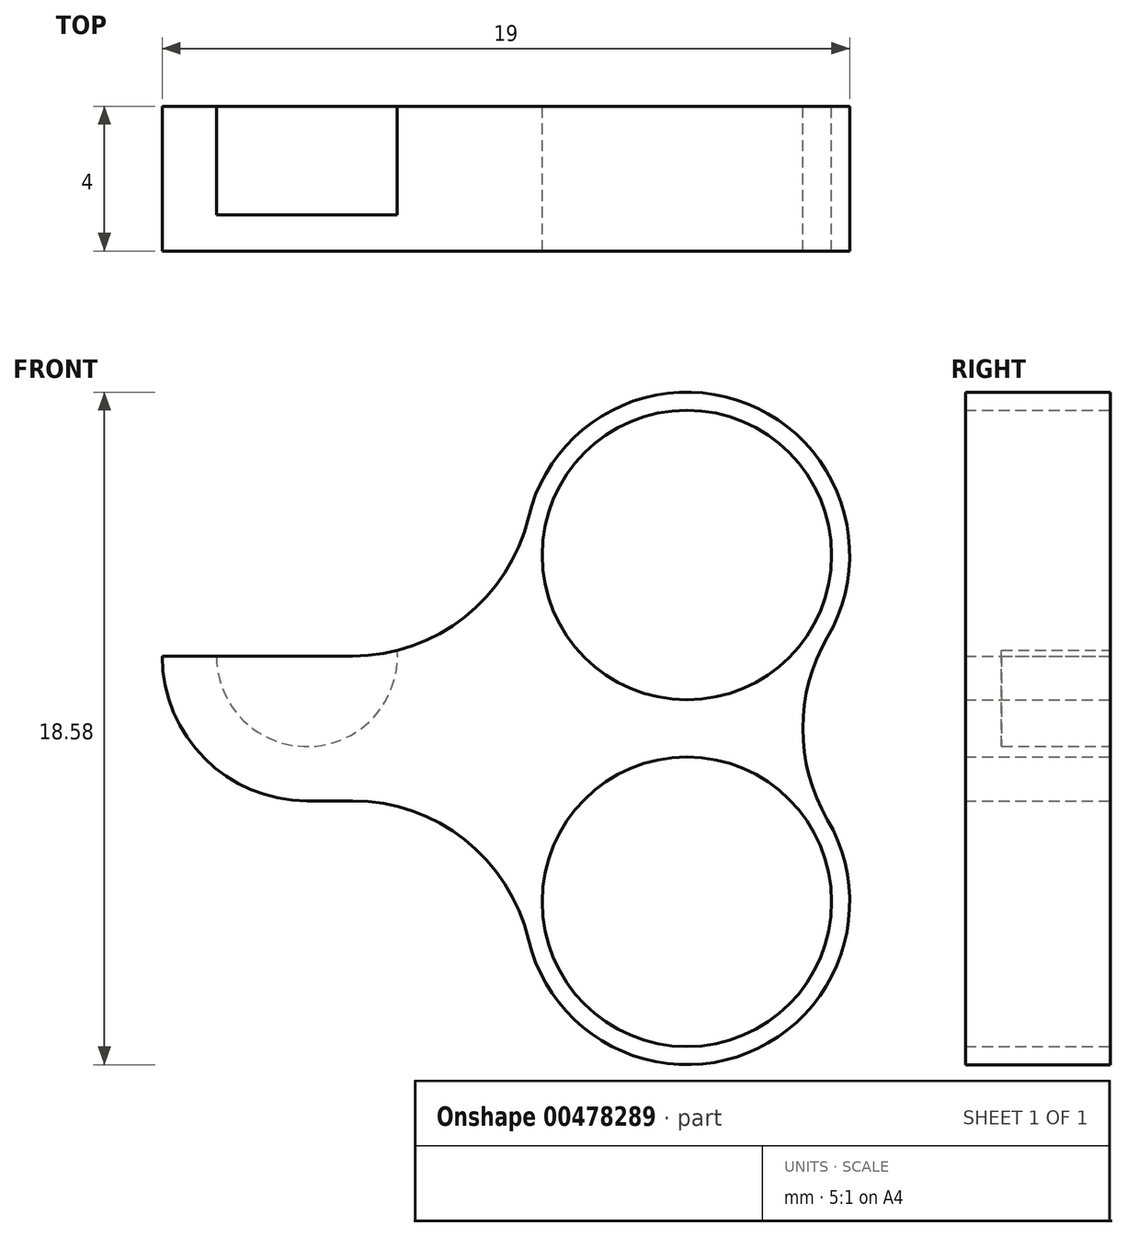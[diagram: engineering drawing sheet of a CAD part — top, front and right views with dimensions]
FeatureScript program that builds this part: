
annotation { "Feature Type Name" : "Feature", "Feature Type Description" : "" }
export const myFeature = defineFeature(function(context is Context, id is Id, definition is map)
    precondition{}
    {
        {
            var Q0;
            Q0=qCreatedBy(makeId("Front.planeOp"),FACE);
            var sketch = newSketch(context, id + "F0", { "sketchPlane" : qUnion([Q0])});
            skLineSegment(sketch, "E0.bottom", {"start": v(-4.5, 4.5) * mm, "end": v(4.5, 4.5) * mm});
            skLineSegment(sketch, "E0.top", {"start": v(-4.5, -14.08) * mm, "end": v(4.5, -14.08) * mm});
            skLineSegment(sketch, "E0.left", {"start": v(-4.5, 4.5) * mm, "end": v(-4.5, -14.08) * mm});
            skLineSegment(sketch, "E0.right", {"start": v(4.5, 4.5) * mm, "end": v(4.5, -14.08) * mm});
            skCircle(sketch, "E1", {"center": v(0, 0) * mm, "radius": 4 * mm});
            skCircle(sketch, "E2", {"center": v(0, -9.58) * mm, "radius": 4 * mm});
            skPoint(sketch, "E3", {"position": v(0, 4.5) * mm});
            skLineSegment(sketch, "E4.bottom", {"start": v(-14.5, -2.79) * mm, "end": v(0, -2.8) * mm});
            skLineSegment(sketch, "E4.left", {"start": v(-14.5, -2.79) * mm, "end": v(-14.5, -6.8) * mm});
            skLineSegment(sketch, "E4.right", {"start": v(0, -2.8) * mm, "end": v(0, -6.8) * mm});
            skLineSegment(sketch, "E5", {"start": v(-14.5, -6.79) * mm, "end": v(0, -6.8) * mm});
            skPoint(sketch, "E6", {"position": v(-10.5, -2.79) * mm});
            skCircle(sketch, "E7", {"center": v(-10.5, -2.79) * mm, "radius": 2.5 * mm});
            skPoint(sketch, "E8", {"position": v(0, -4.8) * mm});
            skCircle(sketch, "E9.0", {"center": v(0, 0) * mm, "radius": 4.5 * mm});
            skCircle(sketch, "E10.0", {"center": v(0, -9.58) * mm, "radius": 4.5 * mm});
            skPoint(sketch, "E11", {"position": v(4.5, -4.8) * mm});
            skCircle(sketch, "E12", {"center": v(8.2, -4.79) * mm, "radius": 5 * mm});
            skSolve(sketch);
        }
        {
            var Q0;
            {var subQ5=sQuery(id+"F0.wireOp",EDGE,"E4.left");Q0=makeQuery(id+"F0.imprint","IMPRINT",FACE,{"disambiguationData":[TD([[makeQuery(id+"F0.imprint","IMPRINT",EDGE,{"derivedFrom":subQ5}),1.0]])]});}
            var Q1;
            {var subQ0=sQuery(id+"F0.wireOp",EDGE,"E7");var subQ1=sQuery(id+"F0.wireOp",EDGE,"E4.bottom");var subQ2=makeQuery(id+"F0.imprint","INTERSECT",VERTEX,{"disambiguationData":[OD(0.0)],"derivedFrom":[subQ1,subQ0]});Q1=makeQuery(id+"F0.imprint","IMPRINT",FACE,{"disambiguationData":[TD([[makeQuery(id+"F0.imprint","IMPRINT",EDGE,{"disambiguationData":[TD([[subQ2,-1.0]])],"derivedFrom":subQ1}),-1.0]])]});}
            var Q2;
            {var subQ0=sQuery(id+"F0.wireOp",EDGE,"E4.bottom");var subQ1=sQuery(id+"F0.wireOp",EDGE,"E0.left");var subQ2=makeQuery(id+"F0.imprint","INTERSECT",VERTEX,{"derivedFrom":[subQ1,subQ0]});Q2=makeQuery(id+"F0.imprint","IMPRINT",FACE,{"disambiguationData":[TD([[makeQuery(id+"F0.imprint","IMPRINT",EDGE,{"disambiguationData":[TD([[subQ2,-1.0]])],"derivedFrom":subQ1}),1.0]])]});}
            var Q3;
            {var subQ2=sQuery(id+"F0.wireOp",EDGE,"E4.bottom");var subQ7=sQuery(id+"F0.wireOp",EDGE,"E1");var subQ8=makeQuery(id+"F0.imprint","INTERSECT",VERTEX,{"derivedFrom":[subQ7,subQ2]});Q3=makeQuery(id+"F0.imprint","IMPRINT",FACE,{"disambiguationData":[TD([[makeQuery(id+"F0.imprint","IMPRINT",EDGE,{"disambiguationData":[TD([[subQ8,1.0]])],"derivedFrom":subQ7}),-1.0]])]});}
            var Q4;
            {var subQ0=sQuery(id+"F0.wireOp",EDGE,"E4.bottom");var subQ1=sQuery(id+"F0.wireOp",EDGE,"E1");var subQ2=makeQuery(id+"F0.imprint","INTERSECT",VERTEX,{"derivedFrom":[subQ1,subQ0]});Q4=makeQuery(id+"F0.imprint","IMPRINT",FACE,{"disambiguationData":[TD([[makeQuery(id+"F0.imprint","IMPRINT",EDGE,{"disambiguationData":[TD([[subQ2,-1.0]])],"derivedFrom":subQ1}),-1.0]])]});}
            var Q5;
            {var subQ0=sQuery(id+"F0.wireOp",EDGE,"E4.right");var subQ1=sQuery(id+"F0.wireOp",EDGE,"E2");var subQ2=makeQuery(id+"F0.imprint","INTERSECT",VERTEX,{"derivedFrom":[subQ1,subQ0]});Q5=makeQuery(id+"F0.imprint","IMPRINT",FACE,{"disambiguationData":[TD([[makeQuery(id+"F0.imprint","IMPRINT",EDGE,{"disambiguationData":[TD([[subQ2,-1.0]])],"derivedFrom":subQ1}),-1.0]])]});}
            var Q6;
            {var subQ8=sQuery(id+"F0.wireOp",EDGE,"E4.right");var subQ10=sQuery(id+"F0.wireOp",EDGE,"E2");var subQ11=makeQuery(id+"F0.imprint","INTERSECT",VERTEX,{"derivedFrom":[subQ10,subQ8]});Q6=makeQuery(id+"F0.imprint","IMPRINT",FACE,{"disambiguationData":[TD([[makeQuery(id+"F0.imprint","IMPRINT",EDGE,{"disambiguationData":[TD([[subQ11,1.0]])],"derivedFrom":subQ10}),-1.0]])]});}
            var Q7;
            {var subQ0=sQuery(id+"F0.wireOp",EDGE,"E5");var subQ1=sQuery(id+"F0.wireOp",EDGE,"E0.left");var subQ2=makeQuery(id+"F0.imprint","INTERSECT",VERTEX,{"derivedFrom":[subQ1,subQ0]});Q7=makeQuery(id+"F0.imprint","IMPRINT",FACE,{"disambiguationData":[TD([[makeQuery(id+"F0.imprint","IMPRINT",EDGE,{"disambiguationData":[TD([[subQ2,-1.0]])],"derivedFrom":subQ1}),1.0]])]});}
            var Q8;
            {var subQ0=sQuery(id+"F0.wireOp",EDGE,"YeDadiRC-dy8C-tnKM-ttN9-oYbZLPGVziEG");var subQ1=sQuery(id+"F0.wireOp",EDGE,"h8KZgrjz-lG1N-5C4Z-7fBZ-zu0OKHp02DLF");var subQ2=makeQuery(id+"F0.imprint","INTERSECT",VERTEX,{"disambiguationData":[OD(0.0)],"derivedFrom":[subQ1,subQ0]});Q8=makeQuery(id+"F0.imprint","IMPRINT",FACE,{"disambiguationData":[TD([[makeQuery(id+"F0.imprint","IMPRINT",EDGE,{"disambiguationData":[TD([[subQ2,-1.0]])],"derivedFrom":subQ1}),1.0]])]});}
            var Q9;
            {var subQ0=sQuery(id+"F0.wireOp",EDGE,"G7RmqFI7-FwWg-S7XD-UXWy-2U9f1rseJs2D");var subQ1=sQuery(id+"F0.wireOp",EDGE,"h8KZgrjz-lG1N-5C4Z-7fBZ-zu0OKHp02DLF");var subQ2=makeQuery(id+"F0.imprint","INTERSECT",VERTEX,{"derivedFrom":[subQ1,subQ0]});Q9=makeQuery(id+"F0.imprint","IMPRINT",FACE,{"disambiguationData":[TD([[makeQuery(id+"F0.imprint","IMPRINT",EDGE,{"disambiguationData":[TD([[subQ2,-1.0]])],"derivedFrom":subQ1}),-1.0]])]});}
            var Q10;
            {var subQ0=sQuery(id+"F0.wireOp",EDGE,"E9.0");var subQ1=sQuery(id+"F0.wireOp",EDGE,"E0.left");var subQ2=makeQuery(id+"F0.imprint","INTERSECT",VERTEX,{"derivedFrom":[subQ1,subQ0]});Q10=makeQuery(id+"F0.imprint","IMPRINT",FACE,{"disambiguationData":[TD([[makeQuery(id+"F0.imprint","IMPRINT",EDGE,{"disambiguationData":[TD([[subQ2,-1.0]])],"derivedFrom":subQ1}),1.0]])]});}
            var Q11;
            {var subQ0=sQuery(id+"F0.wireOp",EDGE,"E9.0");var subQ1=sQuery(id+"F0.wireOp",EDGE,"E4.right");var subQ2=makeQuery(id+"F0.imprint","INTERSECT",VERTEX,{"derivedFrom":[subQ1,subQ0]});Q11=makeQuery(id+"F0.imprint","IMPRINT",FACE,{"disambiguationData":[TD([[makeQuery(id+"F0.imprint","IMPRINT",EDGE,{"disambiguationData":[TD([[subQ2,-1.0]])],"derivedFrom":subQ1}),1.0]])]});}
            extrude(context, id + "F1", {"entities" : qUnion([Q0, Q1, Q2, Q3, Q4, Q5, Q6, Q7, Q8, Q9, Q10, Q11]), "depth" : 4 * mm});
        }
        {
            var Q0;
            Q0=makeQuery(id+"F1.opExtrude","SWEPT_EDGE",EDGE,{"disambiguationData":[OSD([sQuery(id+"F0.wireOp",EDGE,"E0.left"),sQuery(id+"F0.wireOp",EDGE,"E4.bottom")])]});
            var Q1;
            Q1=makeQuery(id+"F1.opExtrude","SWEPT_EDGE",EDGE,{"disambiguationData":[OSD([sQuery(id+"F0.wireOp",EDGE,"E0.left"),sQuery(id+"F0.wireOp",EDGE,"E5")])]});
            fillet(context, id + "F2", {"entities" : qUnion([Q0, Q1]), "radius" : 5 * mm, "tangentPropagation" : true, "allowEdgeOverflow" : false});
        }
        {
            var Q0;
            Q0=makeQuery(id+"F1.opExtrude","SWEPT_EDGE",EDGE,{"disambiguationData":[OSD([sQuery(id+"F0.wireOp",EDGE,"E4.left"),sQuery(id+"F0.wireOp",EDGE,"E5")])]});
            fillet(context, id + "F3", {"entities" : qUnion([Q0]), "radius" : 4 * mm, "tangentPropagation" : true, "allowEdgeOverflow" : false});
        }
        {
            var Q0;
            {var subQ0=sQuery(id+"F0.wireOp",EDGE,"E7");var subQ1=sQuery(id+"F0.wireOp",EDGE,"E4.bottom");var subQ2=makeQuery(id+"F0.imprint","INTERSECT",VERTEX,{"disambiguationData":[OD(0.0)],"derivedFrom":[subQ1,subQ0]});Q0=makeQuery(id+"F0.imprint","IMPRINT",FACE,{"disambiguationData":[TD([[makeQuery(id+"F0.imprint","IMPRINT",EDGE,{"disambiguationData":[TD([[subQ2,-1.0]])],"derivedFrom":subQ1}),-1.0]])]});}
            var Q1;
            {var subQ0=sQuery(id+"F0.wireOp",EDGE,"E7");var subQ1=sQuery(id+"F0.wireOp",EDGE,"E4.bottom");var subQ2=makeQuery(id+"F0.imprint","INTERSECT",VERTEX,{"disambiguationData":[OD(0.0)],"derivedFrom":[subQ1,subQ0]});Q1=makeQuery(id+"F0.imprint","IMPRINT",FACE,{"disambiguationData":[TD([[makeQuery(id+"F0.imprint","IMPRINT",EDGE,{"disambiguationData":[TD([[subQ2,-1.0]])],"derivedFrom":subQ1}),1.0]])]});}
            extrude(context, id + "F4", {"entities" : qUnion([Q0, Q1]), "operationType" : NewBodyOperationType.REMOVE, "depth" : 3 * mm});
        }
    });
